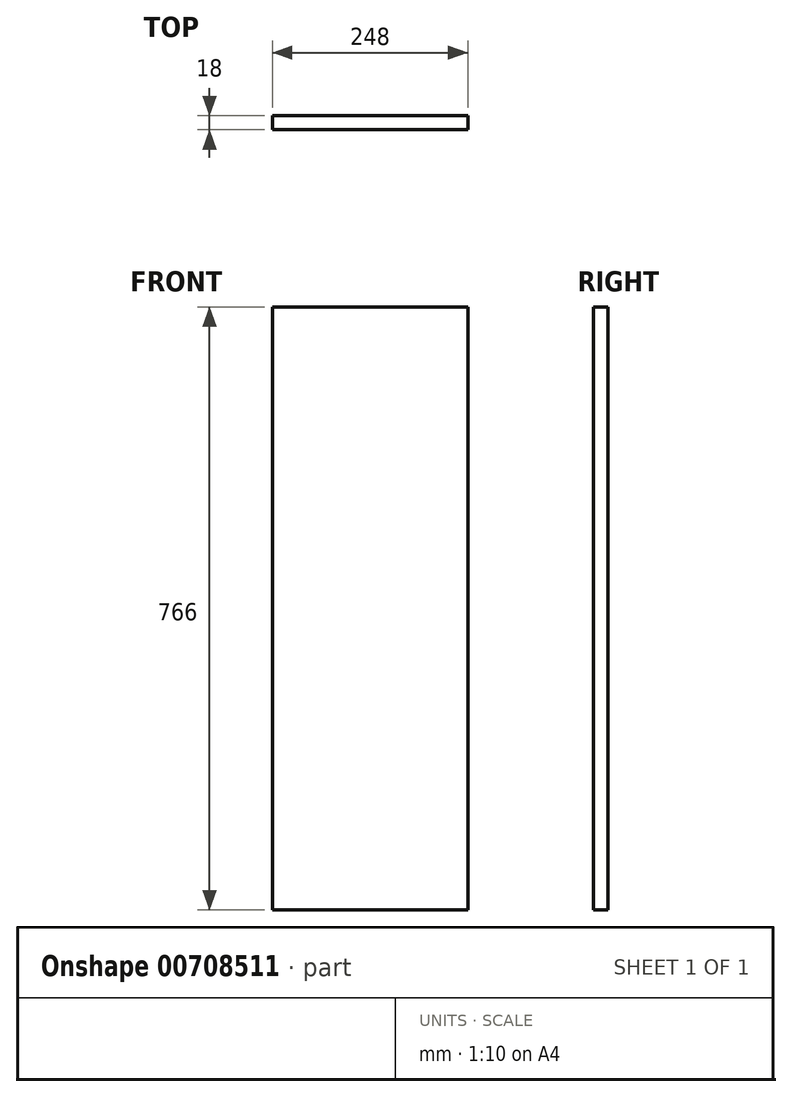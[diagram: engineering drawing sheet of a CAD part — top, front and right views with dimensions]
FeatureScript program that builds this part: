
annotation { "Feature Type Name" : "Feature", "Feature Type Description" : "" }
export const myFeature = defineFeature(function(context is Context, id is Id, definition is map)
    precondition{}
    {
        {
            var Q0;
            Q0=qCreatedBy(makeId("Front.planeOp"),FACE);
            var sketch = newSketch(context, id + "F0", { "sketchPlane" : qUnion([Q0])});
            skLineSegment(sketch, "E0.bottom", {"start": v(0, 0) * mm, "end": v(-248, 0) * mm});
            skLineSegment(sketch, "E0.top", {"start": v(0, -766) * mm, "end": v(-248, -766) * mm});
            skLineSegment(sketch, "E0.left", {"start": v(0, 0) * mm, "end": v(0, -766) * mm});
            skLineSegment(sketch, "E0.right", {"start": v(-248, 0) * mm, "end": v(-248, -766) * mm});
            skSolve(sketch);
        }
        {
            var Q0;
            Q0=qSketchRegion(id+"F0",true);
            extrude(context, id + "F1", {"entities" : qUnion([Q0]), "depth" : 18 * mm, "offsetDistance" : 25 * mm});
        }
    });
